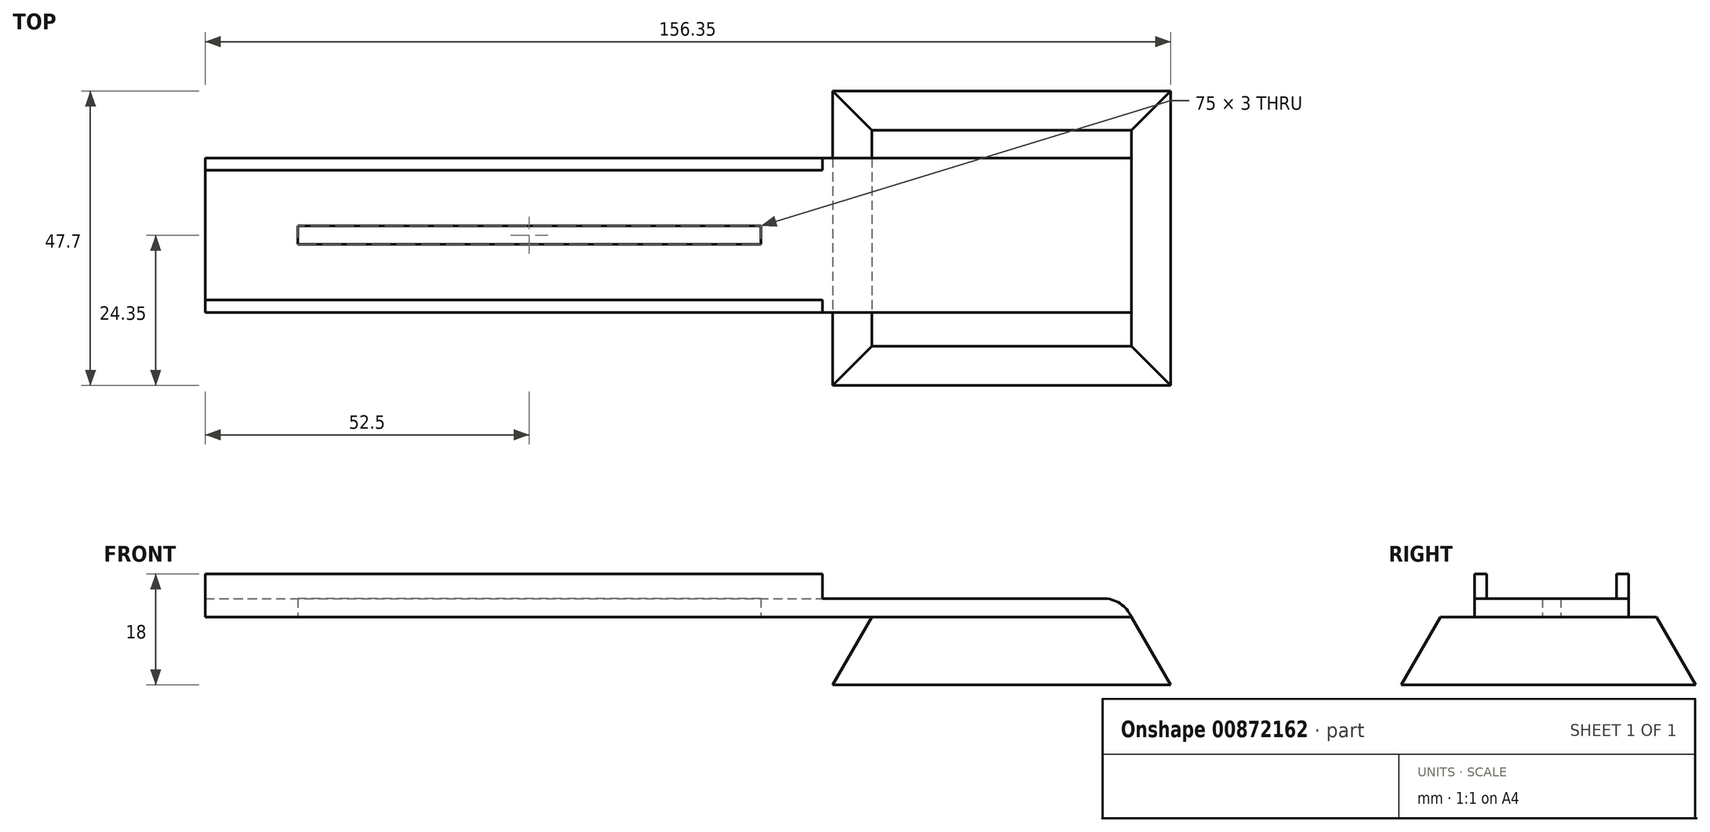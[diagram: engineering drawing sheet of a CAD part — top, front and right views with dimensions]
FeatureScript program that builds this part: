
annotation { "Feature Type Name" : "Feature", "Feature Type Description" : "" }
export const myFeature = defineFeature(function(context is Context, id is Id, definition is map)
    precondition{}
    {
        {
            var Q0;
            Q0=qCreatedBy(makeId("Top.planeOp"),FACE);
            var sketch = newSketch(context, id + "F0", { "sketchPlane" : qUnion([Q0])});
            skLineSegment(sketch, "E0", {"start": v(0, 0) * mm, "end": v(150, 0) * mm});
            skLineSegment(sketch, "E1", {"start": v(150, 0) * mm, "end": v(150, 25) * mm});
            skLineSegment(sketch, "E2", {"start": v(150, 25) * mm, "end": v(0, 25) * mm});
            skLineSegment(sketch, "E3", {"start": v(0, 25) * mm, "end": v(0, 0) * mm});
            skSolve(sketch);
        }
        {
            var Q0;
            Q0=makeQuery(id+"F0.imprint","IMPRINT",FACE,{"disambiguationData":[TD([[makeQuery(id+"F0.imprint","IMPRINT",EDGE,{"derivedFrom":sQuery(id+"F0.wireOp",EDGE,"E0")}),1.0]])]});
            extrude(context, id + "F1", {"entities" : qUnion([Q0]), "depth" : 3 * mm, "offsetDistance" : 25 * mm});
        }
        {
            var Q0;
            Q0=qCreatedBy(makeId("Top.planeOp"),FACE);
            var sketch = newSketch(context, id + "F2", { "sketchPlane" : qUnion([Q0])});
            skLineSegment(sketch, "E4", {"start": v(0, 0) * mm, "end": v(100, 0) * mm});
            skLineSegment(sketch, "E5", {"start": v(100, 0) * mm, "end": v(100, 2) * mm});
            skLineSegment(sketch, "E6", {"start": v(100, 2) * mm, "end": v(0, 2) * mm});
            skLineSegment(sketch, "E7", {"start": v(0, 2) * mm, "end": v(0, 0) * mm});
            skLineSegment(sketch, "E8", {"start": v(0, 25) * mm, "end": v(100, 25) * mm});
            skLineSegment(sketch, "E9", {"start": v(100, 25) * mm, "end": v(100, 23) * mm});
            skLineSegment(sketch, "E10", {"start": v(100, 23) * mm, "end": v(0, 23) * mm});
            skLineSegment(sketch, "E11", {"start": v(0, 23) * mm, "end": v(0, 25) * mm});
            skSolve(sketch);
        }
        {
            var Q0;
            Q0=makeQuery(id+"F2.imprint","IMPRINT",FACE,{"disambiguationData":[TD([[makeQuery(id+"F2.imprint","IMPRINT",EDGE,{"derivedFrom":sQuery(id+"F2.wireOp",EDGE,"E8")}),-1.0]])]});
            var Q1;
            Q1=makeQuery(id+"F2.imprint","IMPRINT",FACE,{"disambiguationData":[TD([[makeQuery(id+"F2.imprint","IMPRINT",EDGE,{"derivedFrom":sQuery(id+"F2.wireOp",EDGE,"E4")}),1.0]])]});
            extrude(context, id + "F3", {"entities" : qUnion([Q0, Q1]), "operationType" : NewBodyOperationType.ADD, "depth" : 7 * mm, "offsetDistance" : 25 * mm});
        }
        {
            var Q0;
            Q0=qCreatedBy(makeId("Top.planeOp"),FACE);
            var sketch = newSketch(context, id + "F4", { "sketchPlane" : qUnion([Q0])});
            skLineSegment(sketch, "E12", {"start": v(0, 0) * mm, "end": v(150, 0) * mm});
            skLineSegment(sketch, "E13", {"start": v(150, 0) * mm, "end": v(150, -5.5) * mm});
            skLineSegment(sketch, "E14", {"start": v(150, -5.5) * mm, "end": v(108, -5.5) * mm});
            skLineSegment(sketch, "E15", {"start": v(108, -5.5) * mm, "end": v(108, 29.5) * mm});
            skLineSegment(sketch, "E16", {"start": v(108, 29.5) * mm, "end": v(150, 29.5) * mm});
            skLineSegment(sketch, "E17", {"start": v(150, 29.5) * mm, "end": v(150, 0) * mm});
            skSolve(sketch);
        }
        {
            var Q0;
            {var subQ0=sQuery(id+"F4.wireOp",EDGE,"E13");Q0=makeQuery(id+"F4.imprint","IMPRINT",FACE,{"disambiguationData":[TD([[makeQuery(id+"F4.imprint","IMPRINT",EDGE,{"derivedFrom":subQ0}),-1.0]])]});}
            var Q1;
            {var subQ4=sQuery(id+"F4.wireOp",EDGE,"E16");Q1=makeQuery(id+"F4.imprint","IMPRINT",FACE,{"disambiguationData":[TD([[makeQuery(id+"F4.imprint","IMPRINT",EDGE,{"derivedFrom":subQ4}),-1.0]])]});}
            var Q2;
            Q2=sQuery(id+"F4.wireOp",EDGE,"E15");
            var Q3;
            Q3=sQuery(id+"F4.wireOp",EDGE,"E17");
            var Q4;
            Q4=sQuery(id+"F4.wireOp",EDGE,"E14");
            var Q5;
            Q5=sQuery(id+"F4.wireOp",EDGE,"E16");
            var Q6;
            Q6=sQuery(id+"F4.wireOp",EDGE,"E13");
            extrude(context, id + "F5", {"entities" : qUnion([Q0, Q1]), "operationType" : NewBodyOperationType.ADD, "surfaceEntities" : qUnion([Q2, Q3, Q4, Q5, Q6]), "oppositeDirection" : true, "depth" : 11 * mm, "offsetDistance" : 25 * mm, "hasDraft" : true, "draftAngle" : 30 * degree});
        }
        {
            var Q0;
            Q0=qCreatedBy(makeId("Top.planeOp"),FACE);
            var sketch = newSketch(context, id + "F6", { "sketchPlane" : qUnion([Q0])});
            skLineSegment(sketch, "E18", {"start": v(0, 0) * mm, "end": v(0, 11) * mm});
            skLineSegment(sketch, "E19", {"start": v(15, 11) * mm, "end": v(90, 11) * mm});
            skLineSegment(sketch, "E20", {"start": v(90, 11) * mm, "end": v(90, 14) * mm});
            skLineSegment(sketch, "E21", {"start": v(90, 14) * mm, "end": v(15, 14) * mm});
            skLineSegment(sketch, "E22", {"start": v(15, 14) * mm, "end": v(15, 11) * mm});
            skSolve(sketch);
        }
        {
            var Q0;
            Q0 = qSketchRegion(id + "F6", true);
            extrude(context, id + "F7", {"entities" : qUnion([Q0]), "operationType" : NewBodyOperationType.REMOVE, "endBound" : BoundingType.THROUGH_ALL, "depth" : 25 * mm, "offsetDistance" : 25 * mm});
        }
        {
            var Q0;
            Q0=makeQuery(id+"F1.opExtrude","CAP_EDGE",EDGE,{"disambiguationData":[OSD([sQuery(id+"F0.wireOp",EDGE,"E1")])],"isStart":false});
            fillet(context, id + "F8", {"entities" : qUnion([Q0]), "radius" : 5 * mm, "tangentPropagation" : true, "allowEdgeOverflow" : false});
        }
    });
